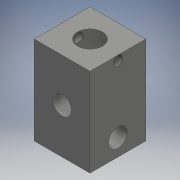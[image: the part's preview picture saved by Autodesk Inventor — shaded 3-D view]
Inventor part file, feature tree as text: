
AUTODESK INVENTOR PART (.ipt)
format: ipt  version: 2018 (Build 220112000, 112)  size: 123,392 bytes
history: native  units: mm
features: sketch x5, hole x4, extrude x1
ambient origin geometry x8: Origin, YZ Plane, XZ Plane, XY Plane, X Axis, Y Axis, Z Axis, Center Point
bodies: Solid1 (feature_tree)
feature tree (10):
  extrude  "Extrusion1"  Depth=36.0mm
  hole  "Hole1"  [1 undecoded]
  hole  "Hole2"  [1 undecoded]
  hole  "Hole3"  [1 undecoded]
  hole  "Hole4"  [1 undecoded]
  sketch  "Sketch1"  dims[d0=36.0mm d1=36.0mm]
  sketch  "Sketch2"  dims[d2=57.0mm d3=0.0mm d4=16.0mm]
  sketch  "Sketch3"  dims[d5=16.0mm d6=6.0mm d7=4.0mm d8=2.0mm d9=90.0deg d10=17.0mm d11=0.0mm]
  sketch  "Sketch4"  dims[d14=12.0mm d15=6.0mm d16=4.0mm d17=2.0mm d18=90.0deg d19=6.0mm d20=0.0mm]
  sketch  "Sketch5"  dims[d23=12.0mm d24=6.0mm d25=4.0mm d26=2.0mm d27=90.0deg d28=6.0mm d29=0.0mm d33=6.0mm d34=6.0mm d35=4.0mm d36=2.0mm d37=90.0deg d38=6.0mm d39=0.0mm d41=6.0mm d43=12.0mm d46=12.0mm]
note: 4 required parameter values undecoded (feature->parameter linkage not recoverable at this tier; creation-order binding heuristic only, values carry confidence <= 0.55)
